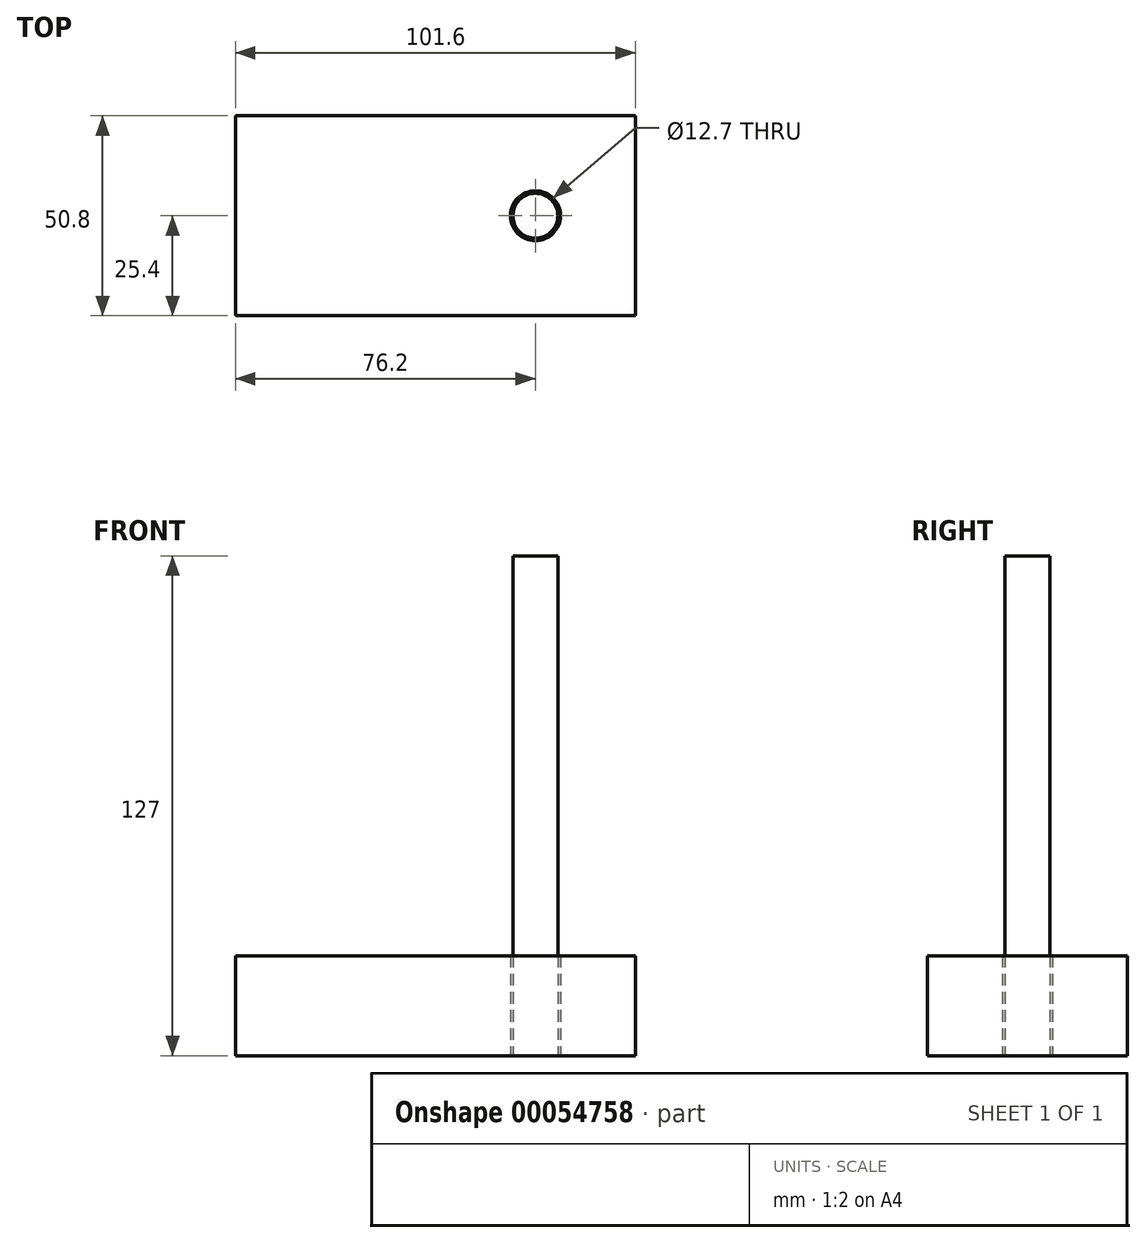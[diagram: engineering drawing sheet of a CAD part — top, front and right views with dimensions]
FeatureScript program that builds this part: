
annotation { "Feature Type Name" : "Feature", "Feature Type Description" : "" }
export const myFeature = defineFeature(function(context is Context, id is Id, definition is map)
    precondition{}
    {
        {
            var Q0;
            Q0=qCreatedBy(makeId("Top.planeOp"),FACE);
            var sketch = newSketch(context, id + "F0", { "sketchPlane" : qUnion([Q0])});
            skLineSegment(sketch, "E0.bottom", {"start": v(-50.8, 25.4) * mm, "end": v(50.8, 25.4) * mm});
            skLineSegment(sketch, "E0.top", {"start": v(-50.8, -25.4) * mm, "end": v(50.8, -25.4) * mm});
            skLineSegment(sketch, "E0.left", {"start": v(-50.8, 25.4) * mm, "end": v(-50.8, -25.4) * mm});
            skLineSegment(sketch, "E0.right", {"start": v(50.8, 25.4) * mm, "end": v(50.8, -25.4) * mm});
            skCircle(sketch, "E1", {"center": v(25.4, 0) * mm, "radius": 6.35 * mm});
            skSolve(sketch);
        }
        {
            var Q0;
            Q0=makeQuery(id+"F0.imprint","IMPRINT",FACE,{"disambiguationData":[TD([[makeQuery(id+"F0.imprint","IMPRINT",EDGE,{"derivedFrom":sQuery(id+"F0.wireOp",EDGE,"E0.bottom")}),-1.0]])]});
            extrude(context, id + "F1", {"entities" : qUnion([Q0]), "depth" : 25.4 * mm});
        }
        {
            var Q0;
            Q0=makeQuery(id+"F0.imprint","IMPRINT",FACE,{"disambiguationData":[TD([[makeQuery(id+"F0.imprint","IMPRINT",EDGE,{"derivedFrom":sQuery(id+"F0.wireOp",EDGE,"E1")}),1.0]])]});
            var sketch = newSketch(context, id + "F2", { "sketchPlane" : qUnion([Q0])});
            skCircle(sketch, "E2", {"center": v(25.38, 0) * mm, "radius": 5.72 * mm});
            skSolve(sketch);
        }
        {
            var Q0;
            Q0=makeQuery(id+"F2.imprint","IMPRINT",FACE,{"disambiguationData":[TD([[makeQuery(id+"F2.imprint","IMPRINT",EDGE,{"derivedFrom":sQuery(id+"F2.wireOp",EDGE,"E2")}),1.0]])]});
            extrude(context, id + "F3", {"entities" : qUnion([Q0]), "depth" : 127 * mm});
        }
    });
